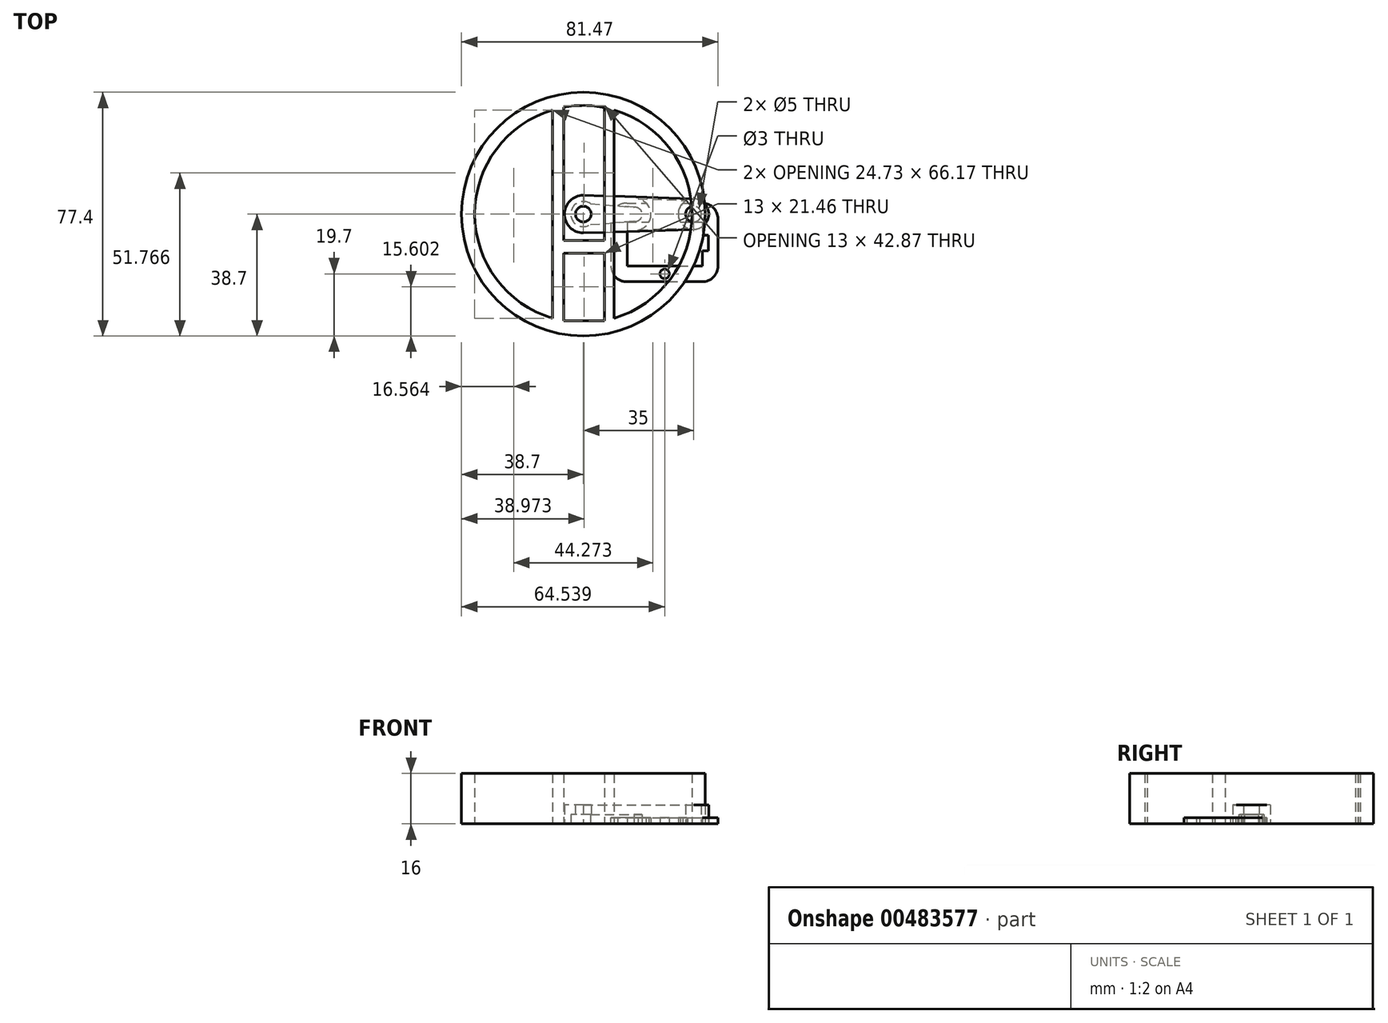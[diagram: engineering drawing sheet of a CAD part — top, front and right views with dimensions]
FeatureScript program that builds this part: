
annotation { "Feature Type Name" : "Feature", "Feature Type Description" : "" }
export const myFeature = defineFeature(function(context is Context, id is Id, definition is map)
    precondition{}
    {
        {
            var Q0;
            Q0=qCreatedBy(makeId("Top.planeOp"),FACE);
            var sketch = newSketch(context, id + "F0", { "sketchPlane" : qUnion([Q0])});
            skLineSegment(sketch, "E0.bottom", {"start": v(13.77, 3.5) * mm, "end": v(37.77, 3.5) * mm});
            skLineSegment(sketch, "E0.top", {"start": v(13.77, -21.5) * mm, "end": v(37.77, -21.5) * mm});
            skLineSegment(sketch, "E0.left", {"start": v(8.77, -1.5) * mm, "end": v(8.77, -16.5) * mm});
            skLineSegment(sketch, "E0.right", {"start": v(42.77, -1.5) * mm, "end": v(42.77, -16.5) * mm});
            skPoint(sketch, "E1.visualSharp", {"position": v(8.77, 3.5) * mm});
            skArc(sketch, "E1.filletArc", {"start": v(13.77, 3.5) * mm, "mid": v(10.24, 2.04) * mm, "end": v(8.77, -1.5) * mm});
            skPoint(sketch, "E2.visualSharp", {"position": v(42.77, 3.5) * mm});
            skArc(sketch, "E2.filletArc", {"start": v(42.77, -1.5) * mm, "mid": v(41.3, 2.04) * mm, "end": v(37.77, 3.5) * mm});
            skPoint(sketch, "E3.visualSharp", {"position": v(42.77, -21.5) * mm});
            skArc(sketch, "E3.filletArc", {"start": v(37.77, -21.5) * mm, "mid": v(41.3, -20.04) * mm, "end": v(42.77, -16.5) * mm});
            skPoint(sketch, "E4.visualSharp", {"position": v(8.77, -21.5) * mm});
            skArc(sketch, "E4.filletArc", {"start": v(8.77, -16.5) * mm, "mid": v(10.24, -20.04) * mm, "end": v(13.77, -21.5) * mm});
            skLineSegment(sketch, "E5.bottom", {"start": v(13.9, -2.5) * mm, "end": v(37.77, -2.5) * mm});
            skLineSegment(sketch, "E5.top", {"start": v(13.9, -16.5) * mm, "end": v(37.77, -16.5) * mm});
            skLineSegment(sketch, "E5.left", {"start": v(13.9, -2.5) * mm, "end": v(13.9, -16.5) * mm});
            skLineSegment(sketch, "E5.right", {"start": v(37.77, -2.5) * mm, "end": v(37.77, -16.5) * mm});
            skCircle(sketch, "E6", {"center": v(25.84, 0) * mm, "radius": 1.5 * mm});
            skPoint(sketch, "E6.centerSnap0", {"position": v(25.84, -2.5) * mm});
            skCircle(sketch, "E7", {"center": v(25.84, -19) * mm, "radius": 1.5 * mm});
            skPoint(sketch, "E7.centerSnap0", {"position": v(25.84, -16.5) * mm});
            skLineSegment(sketch, "E8.bottom", {"start": v(37.77, -6.7) * mm, "end": v(39.77, -6.7) * mm});
            skLineSegment(sketch, "E8.top", {"start": v(37.77, -11.7) * mm, "end": v(39.77, -11.7) * mm});
            skLineSegment(sketch, "E8.left", {"start": v(37.77, -6.7) * mm, "end": v(37.77, -11.7) * mm});
            skLineSegment(sketch, "E8.right", {"start": v(39.77, -6.7) * mm, "end": v(39.77, -11.7) * mm});
            skSolve(sketch);
        }
        {
            var Q0;
            Q0=makeQuery(id+"F0.imprint","IMPRINT",FACE,{"disambiguationData":[TD([[makeQuery(id+"F0.imprint","IMPRINT",EDGE,{"derivedFrom":sQuery(id+"F0.wireOp",EDGE,"E0.bottom")}),-1.0]])]});
            extrude(context, id + "F1", {"entities" : qUnion([Q0]), "depth" : 2 * mm});
        }
        {
            var Q0;
            Q0=qCreatedBy(makeId("Top.planeOp"),FACE);
            var sketch = newSketch(context, id + "F2", { "sketchPlane" : qUnion([Q0])});
            skCircle(sketch, "E9", {"center": v(0, 0) * mm, "radius": 2.5 * mm});
            skCircle(sketch, "E10", {"center": v(35, 0) * mm, "radius": 2.5 * mm});
            skArc(sketch, "E11", {"start": v(0, 6) * mm, "mid": v(-6, 0) * mm, "end": v(0, -6) * mm});
            skCircle(sketch, "E12", {"center": v(35, 0) * mm, "radius": 4.85 * mm});
            skLineSegment(sketch, "E13", {"start": v(0, 6) * mm, "end": v(35.16, 4.85) * mm});
            skLineSegment(sketch, "E14", {"start": v(0, -6) * mm, "end": v(35.16, -4.85) * mm});
            skArc(sketch, "E15", {"start": v(2.21, 3.33) * mm, "mid": v(-4, 0) * mm, "end": v(2.21, -3.33) * mm});
            skLineSegment(sketch, "E16", {"start": v(2.21, 3.33) * mm, "end": v(16.16, 2.12) * mm});
            skLineSegment(sketch, "E17", {"start": v(2.21, -3.33) * mm, "end": v(16.1, -2.28) * mm});
            skArc(sketch, "E18", {"start": v(16.1, -2.28) * mm, "mid": v(18.7, -0.11) * mm, "end": v(16.16, 2.12) * mm});
            skPoint(sketch, "E18.second.point", {"position": v(18.7, 0) * mm});
            skLineSegment(sketch, "E19", {"start": v(16.1, -2.28) * mm, "end": v(17.58, -5.42) * mm});
            skLineSegment(sketch, "E20", {"start": v(16.16, 2.12) * mm, "end": v(17.58, 5.42) * mm});
            skArc(sketch, "E21", {"start": v(17.38, -5) * mm, "mid": v(21.47, -0.06) * mm, "end": v(17.33, 4.84) * mm});
            skLineSegment(sketch, "E22", {"start": v(17.33, 4.84) * mm, "end": v(32.82, 4.33) * mm});
            skLineSegment(sketch, "E23", {"start": v(17.38, -5) * mm, "end": v(33.15, -4.48) * mm});
            skSolve(sketch);
        }
        {
            var Q0;
            {var subQ1=sQuery(id+"F2.wireOp",EDGE,"E11");Q0=makeQuery(id+"F2.imprint","IMPRINT",FACE,{"disambiguationData":[TD([[makeQuery(id+"F2.imprint","IMPRINT",EDGE,{"derivedFrom":subQ1}),1.0]])]});}
            var Q1;
            Q1=makeQuery(id+"F2.imprint","IMPRINT",FACE,{"disambiguationData":[TD([[makeQuery(id+"F2.imprint","IMPRINT",EDGE,{"derivedFrom":sQuery(id+"F2.wireOp",EDGE,"E18")}),-1.0]])]});
            var Q2;
            Q2=makeQuery(id+"F2.imprint","IMPRINT",FACE,{"disambiguationData":[TD([[makeQuery(id+"F2.imprint","IMPRINT",EDGE,{"derivedFrom":sQuery(id+"F2.wireOp",EDGE,"E10")}),-1.0]])]});
            var Q3;
            Q3=makeQuery(id+"F2.imprint","IMPRINT",FACE,{"disambiguationData":[TD([[makeQuery(id+"F2.imprint","IMPRINT",EDGE,{"derivedFrom":sQuery(id+"F2.wireOp",EDGE,"E9")}),-1.0]])]});
            var Q4;
            Q4=makeQuery(id+"F2.imprint","IMPRINT",FACE,{"disambiguationData":[TD([[makeQuery(id+"F2.imprint","IMPRINT",EDGE,{"derivedFrom":sQuery(id+"F2.wireOp",EDGE,"E21")}),-1.0]])]});
            extrude(context, id + "F3", {"entities" : qUnion([Q0, Q1, Q2, Q3, Q4]), "depth" : 6 * mm});
        }
        {
            var Q0;
            {var subQ3=sQuery(id+"F2.wireOp",EDGE,"E22");Q0=makeQuery(id+"F2.imprint","IMPRINT",FACE,{"disambiguationData":[TD([[makeQuery(id+"F2.imprint","IMPRINT",EDGE,{"derivedFrom":subQ3}),1.0]])]});}
            var Q1;
            {var subQ3=sQuery(id+"F2.wireOp",EDGE,"E23");Q1=makeQuery(id+"F2.imprint","IMPRINT",FACE,{"disambiguationData":[TD([[makeQuery(id+"F2.imprint","IMPRINT",EDGE,{"derivedFrom":subQ3}),-1.0]])]});}
            extrude(context, id + "F4", {"entities" : qUnion([Q0, Q1]), "operationType" : NewBodyOperationType.ADD, "depth" : 6 * mm});
        }
        {
            var Q0;
            Q0=makeQuery(id+"F2.imprint","IMPRINT",FACE,{"disambiguationData":[TD([[makeQuery(id+"F2.imprint","IMPRINT",EDGE,{"derivedFrom":sQuery(id+"F2.wireOp",EDGE,"E9")}),-1.0]])]});
            extrude(context, id + "F5", {"entities" : qUnion([Q0]), "operationType" : NewBodyOperationType.REMOVE, "depth" : 3 * mm});
        }
        {
            var Q0;
            Q0=makeQuery(id+"F2.imprint","IMPRINT",FACE,{"disambiguationData":[TD([[makeQuery(id+"F2.imprint","IMPRINT",EDGE,{"derivedFrom":sQuery(id+"F2.wireOp",EDGE,"E21")}),-1.0]])]});
            extrude(context, id + "F6", {"entities" : qUnion([Q0]), "operationType" : NewBodyOperationType.REMOVE, "depth" : 2 * mm});
        }
        {
            var Q0;
            Q0=qCreatedBy(makeId("Top.planeOp"),FACE);
            var sketch = newSketch(context, id + "F7", { "sketchPlane" : qUnion([Q0])});
            skCircle(sketch, "E24", {"center": v(0, 0) * mm, "radius": 34.5 * mm});
            skLineSegment(sketch, "E25.top", {"start": v(-6.23, 22.25) * mm, "end": v(6.77, 22.25) * mm});
            skLineSegment(sketch, "E26", {"start": v(6.77, 22.25) * mm, "end": v(6.77, 33.83) * mm});
            skLineSegment(sketch, "E27", {"start": v(-6.23, 22.25) * mm, "end": v(-6.23, 33.93) * mm});
            skLineSegment(sketch, "E28", {"start": v(9.77, -33.09) * mm, "end": v(9.77, 33.09) * mm});
            skLineSegment(sketch, "E29.bottom", {"start": v(-6.23, 33.93) * mm, "end": v(6.77, 33.93) * mm});
            skLineSegment(sketch, "E30.bottom", {"start": v(6.77, 22.25) * mm, "end": v(-6.23, 22.25) * mm});
            skLineSegment(sketch, "E30.top", {"start": v(6.77, 18.25) * mm, "end": v(-6.23, 18.25) * mm});
            skLineSegment(sketch, "E30.left", {"start": v(6.77, 22.25) * mm, "end": v(6.77, 18.25) * mm});
            skLineSegment(sketch, "E30.right", {"start": v(-6.23, 22.25) * mm, "end": v(-6.23, 18.25) * mm});
            skLineSegment(sketch, "E31.bottom", {"start": v(-6.23, 18.25) * mm, "end": v(6.77, 18.25) * mm});
            skLineSegment(sketch, "E31.top", {"start": v(-6.23, -2.37) * mm, "end": v(6.77, -2.37) * mm});
            skLineSegment(sketch, "E31.left", {"start": v(-6.23, 18.25) * mm, "end": v(-6.23, -2.37) * mm});
            skLineSegment(sketch, "E31.right", {"start": v(6.77, 18.25) * mm, "end": v(6.77, -2.37) * mm});
            skLineSegment(sketch, "E32.bottom", {"start": v(-6.23, -2.37) * mm, "end": v(-3.23, -2.37) * mm});
            skLineSegment(sketch, "E32.top", {"start": v(-6.23, -8.37) * mm, "end": v(-3.23, -8.37) * mm});
            skLineSegment(sketch, "E32.left", {"start": v(-6.23, -2.37) * mm, "end": v(-6.23, -8.37) * mm});
            skLineSegment(sketch, "E32.right", {"start": v(-3.23, -2.37) * mm, "end": v(-3.23, -8.37) * mm});
            skLineSegment(sketch, "E33.bottom", {"start": v(6.77, -2.37) * mm, "end": v(3.77, -2.37) * mm});
            skLineSegment(sketch, "E33.top", {"start": v(6.77, -8.37) * mm, "end": v(3.77, -8.37) * mm});
            skLineSegment(sketch, "E33.left", {"start": v(6.77, -2.37) * mm, "end": v(6.77, -8.37) * mm});
            skLineSegment(sketch, "E33.right", {"start": v(3.77, -2.37) * mm, "end": v(3.77, -8.37) * mm});
            skLineSegment(sketch, "E34.bottom", {"start": v(-6.23, -8.37) * mm, "end": v(6.77, -8.37) * mm});
            skLineSegment(sketch, "E34.top", {"start": v(-6.23, -33.83) * mm, "end": v(6.77, -33.83) * mm});
            skLineSegment(sketch, "E34.left", {"start": v(-6.23, -8.37) * mm, "end": v(-6.23, -33.83) * mm});
            skLineSegment(sketch, "E34.right", {"start": v(6.77, -8.37) * mm, "end": v(6.77, -33.83) * mm});
            skCircle(sketch, "E35", {"center": v(0, 0) * mm, "radius": 38.7 * mm});
            skCircle(sketch, "E36", {"center": v(0, 20.25) * mm, "radius": 0.5 * mm});
            skPoint(sketch, "E36.centerSnap0", {"position": v(6.77, 20.25) * mm});
            skLineSegment(sketch, "E37", {"start": v(-9.77, -33.09) * mm, "end": v(-9.77, 33.09) * mm});
            skLineSegment(sketch, "E38.left", {"start": v(-6.23, -8.37) * mm, "end": v(-6.23, -8.37) * mm});
            skLineSegment(sketch, "E38.right", {"start": v(6.77, -8.37) * mm, "end": v(6.77, -8.37) * mm});
            skLineSegment(sketch, "E39.bottom", {"start": v(6.77, -8.37) * mm, "end": v(-6.23, -8.37) * mm});
            skLineSegment(sketch, "E39.top", {"start": v(6.77, -12.37) * mm, "end": v(-6.23, -12.37) * mm});
            skLineSegment(sketch, "E39.left", {"start": v(6.77, -8.37) * mm, "end": v(6.77, -12.37) * mm});
            skLineSegment(sketch, "E39.right", {"start": v(-6.23, -8.37) * mm, "end": v(-6.23, -12.37) * mm});
            skSolve(sketch);
        }
        {
            var Q0;
            Q0 = qSketchRegion(id + "F7", true);
            var Q1;
            Q1=makeQuery(id+"F7.imprint","IMPRINT",FACE,{"disambiguationData":[TD([[makeQuery(id+"F7.imprint","IMPRINT",EDGE,{"derivedFrom":sQuery(id+"F7.wireOp",EDGE,"E33.bottom")}),1.0]])]});
            var Q2;
            Q2=makeQuery(id+"F7.imprint","IMPRINT",FACE,{"disambiguationData":[TD([[makeQuery(id+"F7.imprint","IMPRINT",EDGE,{"derivedFrom":sQuery(id+"F7.wireOp",EDGE,"E32.bottom")}),-1.0]])]});
            var Q3;
            {var subQ1=sQuery(id+"F7.wireOp",EDGE,"E26");Q3=makeQuery(id+"F7.imprint","IMPRINT",FACE,{"disambiguationData":[TD([[makeQuery(id+"F7.imprint","IMPRINT",EDGE,{"derivedFrom":subQ1}),-1.0]])]});}
            var Q4;
            Q4=makeQuery(id+"F7.imprint","IMPRINT",FACE,{"disambiguationData":[TD([[makeQuery(id+"F7.imprint","IMPRINT",EDGE,{"derivedFrom":sQuery(id+"F7.wireOp",EDGE,"E30.bottom")}),1.0]])]});
            var Q5;
            {var subQ0=sQuery(id+"F7.wireOp",EDGE,"E27");Q5=makeQuery(id+"F7.imprint","IMPRINT",FACE,{"disambiguationData":[TD([[makeQuery(id+"F7.imprint","IMPRINT",EDGE,{"derivedFrom":subQ0}),1.0]])]});}
            var Q6;
            Q6=makeQuery(id+"F7.imprint","IMPRINT",FACE,{"disambiguationData":[TD([[makeQuery(id+"F7.imprint","IMPRINT",EDGE,{"derivedFrom":sQuery(id+"F7.wireOp",EDGE,"E39.top")}),-1.0]])]});
            extrude(context, id + "F8", {"entities" : qUnion([Q0, Q1, Q2, Q3, Q4, Q5, Q6]), "depth" : 16 * mm});
        }
    });
